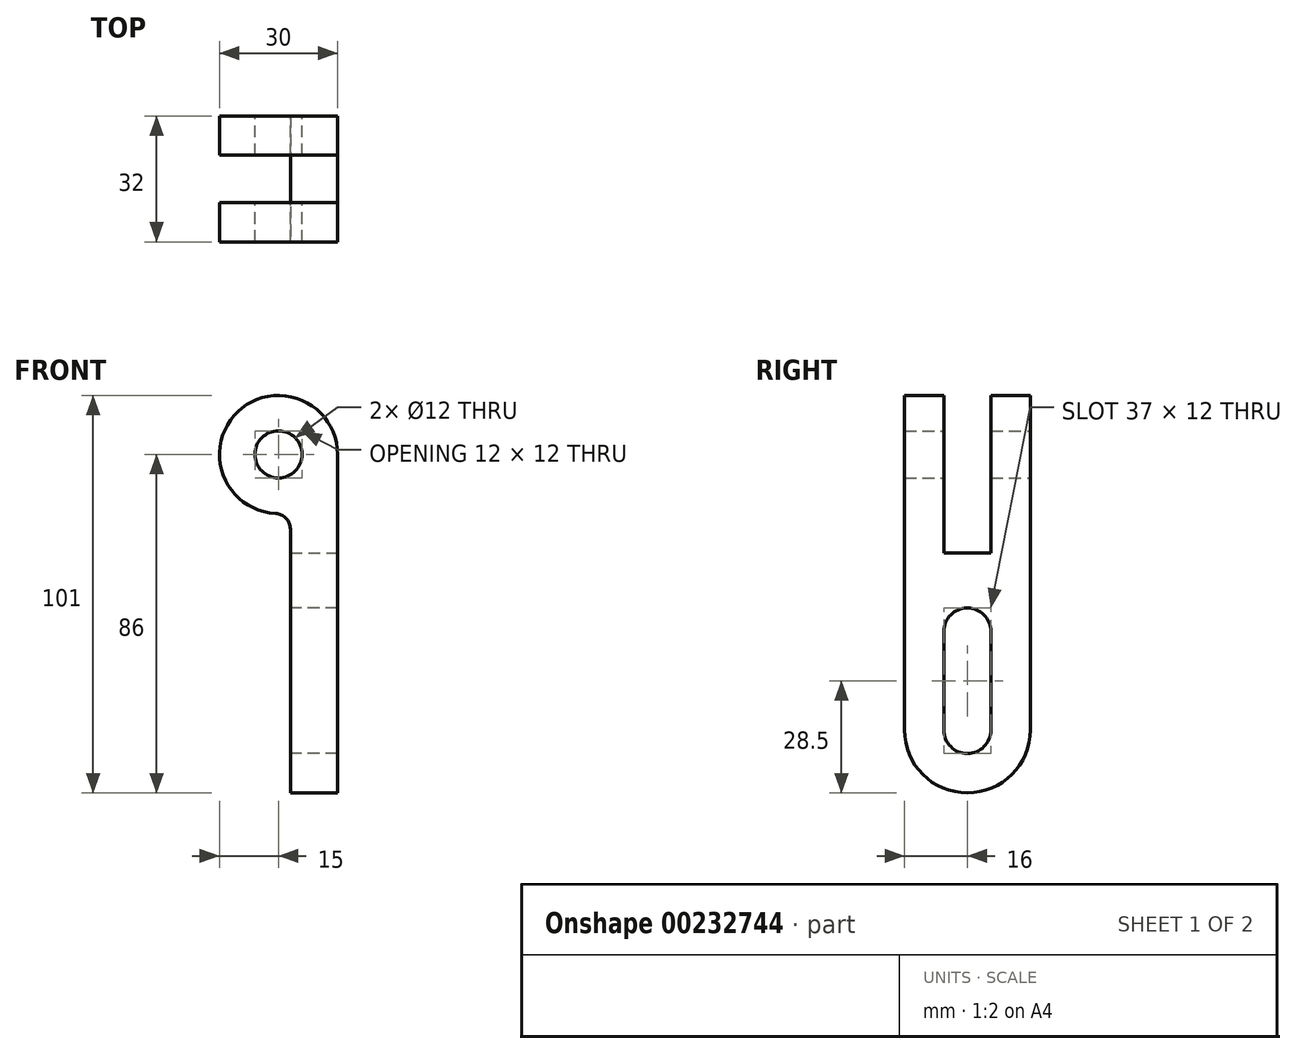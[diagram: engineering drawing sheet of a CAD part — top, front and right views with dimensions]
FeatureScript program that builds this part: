
annotation { "Feature Type Name" : "Feature", "Feature Type Description" : "" }
export const myFeature = defineFeature(function(context is Context, id is Id, definition is map)
    precondition{}
    {
        {
            var Q0;
            Q0=qCreatedBy(makeId("Front.planeOp"),FACE);
            var sketch = newSketch(context, id + "F0", { "sketchPlane" : qUnion([Q0])});
            skArc(sketch, "E0", {"start": v(15, 0) * mm, "mid": v(-10.32, 10.88) * mm, "end": v(-0.79, -14.98) * mm});
            skCircle(sketch, "E1", {"center": v(0, 0) * mm, "radius": 6 * mm});
            skLineSegment(sketch, "E2", {"start": v(-22.65, 0) * mm, "end": v(29.16, 0) * mm, "construction": true});
            skLineSegment(sketch, "E3", {"start": v(0, 22.31) * mm, "end": v(0, -31.52) * mm, "construction": true});
            skLineSegment(sketch, "E4", {"start": v(15, 0) * mm, "end": v(15, -86) * mm});
            skLineSegment(sketch, "E5", {"start": v(-15.35, -70) * mm, "end": v(34.55, -70) * mm, "construction": true});
            skLineSegment(sketch, "E6", {"start": v(15, -86) * mm, "end": v(3, -86) * mm});
            skLineSegment(sketch, "E7", {"start": v(3, -86) * mm, "end": v(3, -18.97) * mm});
            skPoint(sketch, "E8.visualSharp", {"position": v(3, -14.7) * mm});
            skArc(sketch, "E8.filletArc", {"start": v(3, -18.97) * mm, "mid": v(1.9, -16.22) * mm, "end": v(-0.79, -14.98) * mm});
            skSolve(sketch);
        }
        {
            var Q0;
            Q0=makeQuery(id+"F0.imprint","IMPRINT",FACE,{"disambiguationData":[TD([[makeQuery(id+"F0.imprint","IMPRINT",EDGE,{"derivedFrom":sQuery(id+"F0.wireOp",EDGE,"E0")}),1.0]])]});
            extrude(context, id + "F1", {"entities" : qUnion([Q0]), "depth" : 32 * mm});
        }
        {
            var Q0;
            Q0=qCreatedBy(makeId("Right.planeOp"),FACE);
            var sketch = newSketch(context, id + "F2", { "sketchPlane" : qUnion([Q0])});
            skLineSegment(sketch, "E9", {"start": v(-10, -5.18) * mm, "end": v(-10, -25) * mm});
            skLineSegment(sketch, "E10", {"start": v(-22, -16.59) * mm, "end": v(-22, -25) * mm});
            skLineSegment(sketch, "E11", {"start": v(11.3, -25) * mm, "end": v(-43.82, -25) * mm});
            skArc(sketch, "E12", {"start": v(-10, -45) * mm, "mid": v(-16, -39) * mm, "end": v(-22, -45) * mm});
            skArc(sketch, "E13", {"start": v(-22, -70) * mm, "mid": v(-16, -76) * mm, "end": v(-10, -70) * mm});
            skArc(sketch, "E14", {"start": v(-32, -70) * mm, "mid": v(-16, -86) * mm, "end": v(0, -70) * mm});
            skLineSegment(sketch, "E15", {"start": v(-10, -45) * mm, "end": v(-10, -70) * mm});
            skLineSegment(sketch, "E16", {"start": v(-22, -70) * mm, "end": v(-22, -45) * mm});
            skPoint(sketch, "E17.start.orphan", {"position": v(7.66, -45) * mm});
            skPoint(sketch, "E18.trimOffspring.end.orphan", {"position": v(-39.66, -45) * mm});
            skLineSegment(sketch, "E19.trimOffspring", {"start": v(-22, -45) * mm, "end": v(-22, -70) * mm});
            skLineSegment(sketch, "E20.trimOffspring", {"start": v(-10, -84.83) * mm, "end": v(-10, -113.27) * mm});
            skLineSegment(sketch, "E21.trimOffspring", {"start": v(-22, -84.83) * mm, "end": v(-22, -95.62) * mm});
            skSolve(sketch);
        }
        {
            var Q0;
            Q0=makeQuery(id+"F2.imprint","IMPRINT",FACE,{"disambiguationData":[TD([[makeQuery(id+"F2.imprint","IMPRINT",EDGE,{"derivedFrom":sQuery(id+"F2.wireOp",EDGE,"E12")}),1.0]])]});
            extrude(context, id + "F3", {"entities" : qUnion([Q0]), "operationType" : NewBodyOperationType.REMOVE, "endBound" : BoundingType.THROUGH_ALL, "depth" : 25 * mm});
        }
        {
            var Q0;
            Q0=makeQuery(id+"F1.opExtrude","SWEPT_FACE",FACE,{"disambiguationData":[OSD([sQuery(id+"F0.wireOp",EDGE,"E4")])]});
            var sketch = newSketch(context, id + "F4", { "sketchPlane" : qUnion([Q0])});
            skLineSegment(sketch, "E22.0", {"start": v(-32, -86) * mm, "end": v(0, -86) * mm});
            skLineSegment(sketch, "E23.0", {"start": v(-32, 0) * mm, "end": v(-32, -86) * mm});
            skLineSegment(sketch, "E24.0", {"start": v(0, 0) * mm, "end": v(0, -86) * mm});
            skLineSegment(sketch, "E25", {"start": v(-32, 15) * mm, "end": v(0, 15) * mm});
            skLineSegment(sketch, "E26.0", {"start": v(-32, 15) * mm, "end": v(-32, -14.98) * mm});
            skLineSegment(sketch, "E27", {"start": v(-16, -70) * mm, "end": v(3.58, -70) * mm});
            skArc(sketch, "E28", {"start": v(-32, -70) * mm, "mid": v(-16, -86) * mm, "end": v(0, -70) * mm});
            skSolve(sketch);
        }
        {
            var Q0;
            {var subQ0=sQuery(id+"F4.wireOp",EDGE,"E23.0");var subQ1=sQuery(id+"F4.wireOp",EDGE,"E22.0");var subQ2=makeQuery(id+"F4.imprint","INTERSECT",VERTEX,{"derivedFrom":[subQ1,subQ0]});Q0=makeQuery(id+"F4.imprint","IMPRINT",FACE,{"disambiguationData":[TD([[makeQuery(id+"F4.imprint","IMPRINT",EDGE,{"disambiguationData":[TD([[subQ2,-1.0]])],"derivedFrom":subQ1}),1.0]])]});}
            var Q1;
            {var subQ0=sQuery(id+"F4.wireOp",EDGE,"E24.0");var subQ1=sQuery(id+"F4.wireOp",EDGE,"E22.0");var subQ2=makeQuery(id+"F4.imprint","INTERSECT",VERTEX,{"derivedFrom":[subQ1,subQ0]});Q1=makeQuery(id+"F4.imprint","IMPRINT",FACE,{"disambiguationData":[TD([[makeQuery(id+"F4.imprint","IMPRINT",EDGE,{"disambiguationData":[TD([[subQ2,1.0]])],"derivedFrom":subQ1}),1.0]])]});}
            extrude(context, id + "F5", {"entities" : qUnion([Q0, Q1]), "operationType" : NewBodyOperationType.REMOVE, "endBound" : BoundingType.THROUGH_ALL, "oppositeDirection" : true, "depth" : 25 * mm});
        }
        {
            var Q0;
            Q0=makeQuery(id+"F1.opExtrude","SWEPT_FACE",FACE,{"disambiguationData":[OSD([sQuery(id+"F0.wireOp",EDGE,"E4")])]});
            var sketch = newSketch(context, id + "F6", { "sketchPlane" : qUnion([Q0])});
            skLineSegment(sketch, "E29", {"start": v(-22, -25) * mm, "end": v(-22, 16.1) * mm});
            skLineSegment(sketch, "E30", {"start": v(-10, -25) * mm, "end": v(-10, 31.44) * mm});
            skLineSegment(sketch, "E31", {"start": v(-22, -70) * mm, "end": v(13.33, -70) * mm, "construction": true});
            skLineSegment(sketch, "E32", {"start": v(-22, -25) * mm, "end": v(-10, -25) * mm});
            skSolve(sketch);
        }
        {
            var Q0;
            Q0 = qSketchRegion(id + "F6", true);
            var Q1;
            {var subQ0=sQuery(id+"F6.wireOp",EDGE,"E32");Q1=makeQuery(id+"F6.imprint","IMPRINT",FACE,{"disambiguationData":[TD([[makeQuery(id+"F6.imprint","IMPRINT",EDGE,{"derivedFrom":subQ0}),1.0]])]});}
            extrude(context, id + "F7", {"entities" : qUnion([Q0, Q1]), "operationType" : NewBodyOperationType.ADD, "depth" : 25 * mm});
        }
        {
            var Q0;
            Q0=makeQuery(id+"F7.opExtrude","CAP_FACE",FACE,{"disambiguationData":[OSD([sQuery(id+"F0.wireOp",EDGE,"E0"),sQuery(id+"F0.wireOp",EDGE,"E4"),sQuery(id+"F6.wireOp",EDGE,"E29"),sQuery(id+"F6.wireOp",EDGE,"E30"),sQuery(id+"F6.wireOp",EDGE,"E32")])],"isStart":false});
            var sketch = newSketch(context, id + "F8", { "sketchPlane" : qUnion([Q0])});
            skLineSegment(sketch, "E33", {"start": v(-22, 0) * mm, "end": v(-22, 30.9) * mm});
            skLineSegment(sketch, "E34", {"start": v(-22, 30.9) * mm, "end": v(-10, 30.9) * mm});
            skLineSegment(sketch, "E35", {"start": v(-10, 30.9) * mm, "end": v(-10, -2.28) * mm});
            skSolve(sketch);
        }
        {
            var Q0;
            Q0=makeQuery(id+"F8.imprint","IMPRINT",FACE,{"disambiguationData":[TD([[makeQuery(id+"F8.imprint","IMPRINT",EDGE,{"derivedFrom":makeQuery(id+"F7.opExtrude","CAP_EDGE",EDGE,{"disambiguationData":[OSD([sQuery(id+"F6.wireOp",EDGE,"E29")])],"isStart":false})}),-1.0]])]});
            var Q1;
            Q1=makeQuery(id+"F8.imprint","IMPRINT",FACE,{"disambiguationData":[TD([[makeQuery(id+"F8.imprint","IMPRINT",EDGE,{"derivedFrom":sQuery(id+"F8.wireOp",EDGE,"E33")}),-1.0]])]});
            extrude(context, id + "F9", {"entities" : qUnion([Q0, Q1]), "operationType" : NewBodyOperationType.REMOVE, "endBound" : BoundingType.THROUGH_ALL, "oppositeDirection" : true, "depth" : 25 * mm});
        }
    });
